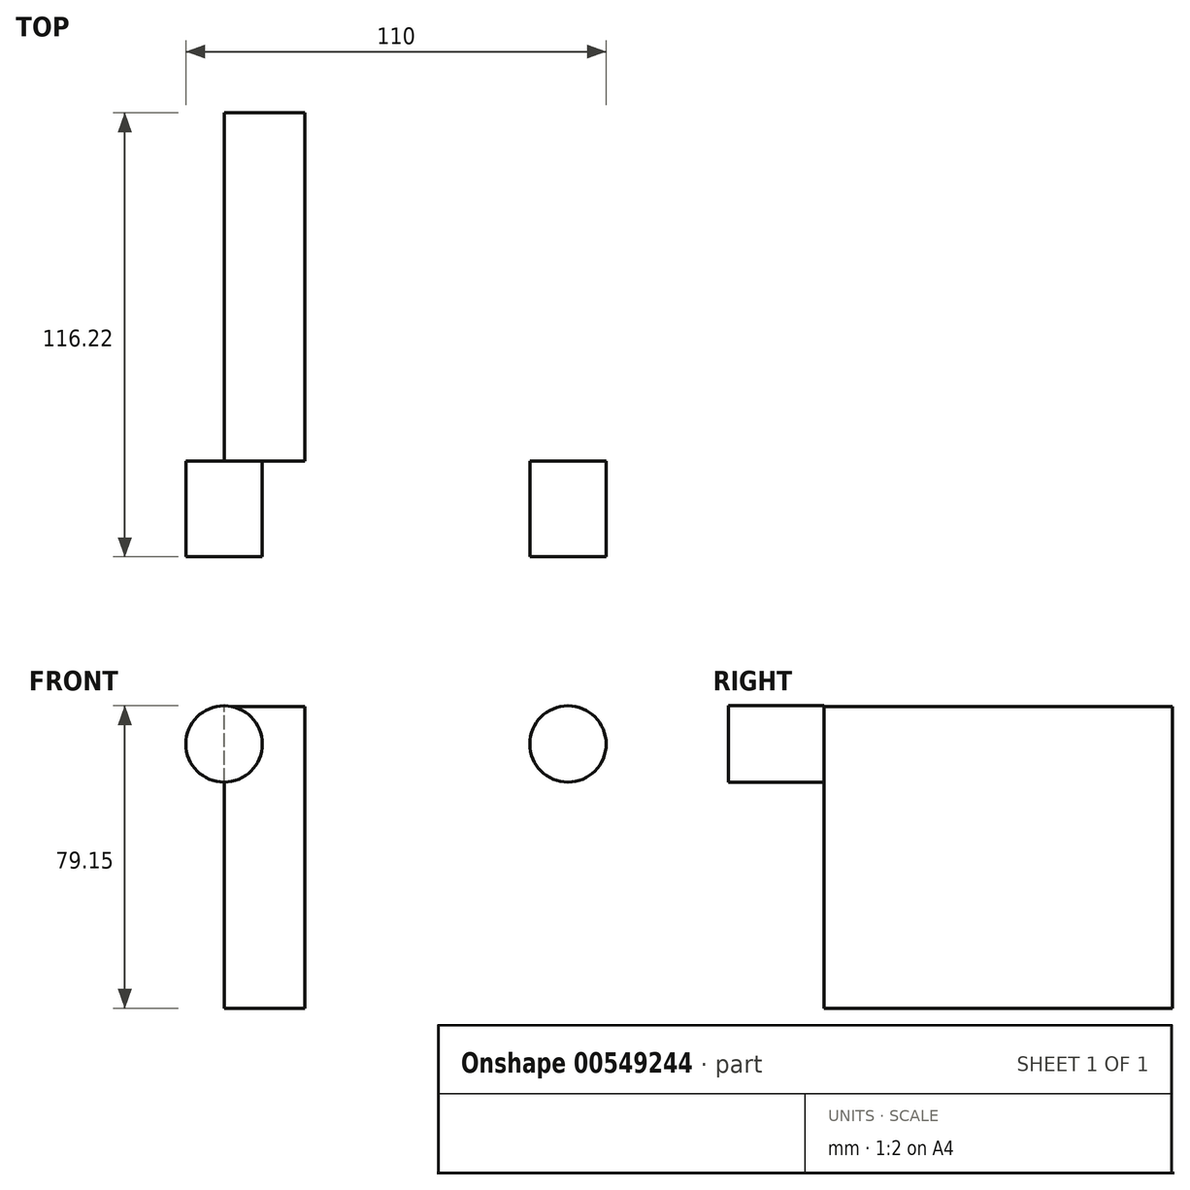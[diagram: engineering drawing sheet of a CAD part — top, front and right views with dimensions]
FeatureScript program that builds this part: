
annotation { "Feature Type Name" : "Feature", "Feature Type Description" : "" }
export const myFeature = defineFeature(function(context is Context, id is Id, definition is map)
    precondition{}
    {
        {
            var Q0;
            Q0=qCreatedBy(makeId("Front.planeOp"),FACE);
            var sketch = newSketch(context, id + "F0", { "sketchPlane" : qUnion([Q0])});
            skCircle(sketch, "E0", {"center": v(0, 0) * mm, "radius": 10 * mm});
            skCircle(sketch, "E1", {"center": v(90, 0) * mm, "radius": 10 * mm});
            skSolve(sketch);
        }
        {
            var Q0;
            Q0 = qSketchRegion(id + "FbC3yILkAgBit30_0", true);
            var Q1;
            {var subQ0=sQuery(id+"FbC3yILkAgBit30_0.wireOp",EDGE,"f8ec6cf9-0aed-454a-bf1e-b6ddcc8805f9");Q1=makeQuery(id+"FbC3yILkAgBit30_0.imprint","IMPRINT",FACE,{"disambiguationData":[TD([[makeQuery(id+"FbC3yILkAgBit30_0.imprint","IMPRINT",EDGE,{"derivedFrom":subQ0}),-1.0]])]});}
            var Q2;
            {var subQ0=sQuery(id+"FbC3yILkAgBit30_0.wireOp",EDGE,"99fb8cbc-f849-4f20-b945-300c9e0049b8");var subQ1=makeQuery(id+"FbC3yILkAgBit30_0.imprint","INTERSECT",VERTEX,{"derivedFrom":[subQ0,sQuery(id+"FbC3yILkAgBit30_0.wireOp",EDGE,"f8ec6cf9-0aed-454a-bf1e-b6ddcc8805f9")]});Q2=makeQuery(id+"FbC3yILkAgBit30_0.imprint","IMPRINT",FACE,{"disambiguationData":[TD([[makeQuery(id+"FbC3yILkAgBit30_0.imprint","IMPRINT",EDGE,{"disambiguationData":[TD([[subQ1,-1.0]])],"derivedFrom":subQ0}),1.0]])]});}
            var Q3;
            Q3 = qSketchRegion(id + "F0", true);
            extrude(context, id + "F1", {"entities" : qUnion([Q0, Q1, Q2, Q3]), "depth" : 25 * mm, "offsetDistance" : 25 * mm});
        }
        {
            var Q0;
            Q0 = qSketchRegion(id + "F0", true);
            var sketch = newSketch(context, id + "F2", { "sketchPlane" : qUnion([Q0])});
            skLineSegment(sketch, "E2.bottom", {"start": v(21.15, -69.15) * mm, "end": v(0, -69.15) * mm});
            skLineSegment(sketch, "E2.top", {"start": v(21.15, 9.77) * mm, "end": v(0, 9.77) * mm});
            skLineSegment(sketch, "E2.left", {"start": v(21.15, -69.15) * mm, "end": v(21.15, 9.77) * mm});
            skLineSegment(sketch, "E2.right", {"start": v(0, -69.15) * mm, "end": v(0, 9.77) * mm});
            skSolve(sketch);
        }
        {
            var Q0;
            Q0 = qSketchRegion(id + "F2", true);
            extrude(context, id + "F3", {"entities" : qUnion([Q0]), "operationType" : NewBodyOperationType.ADD, "oppositeDirection" : true, "depth" : 91.22 * mm, "offsetDistance" : 25 * mm});
        }
    });
